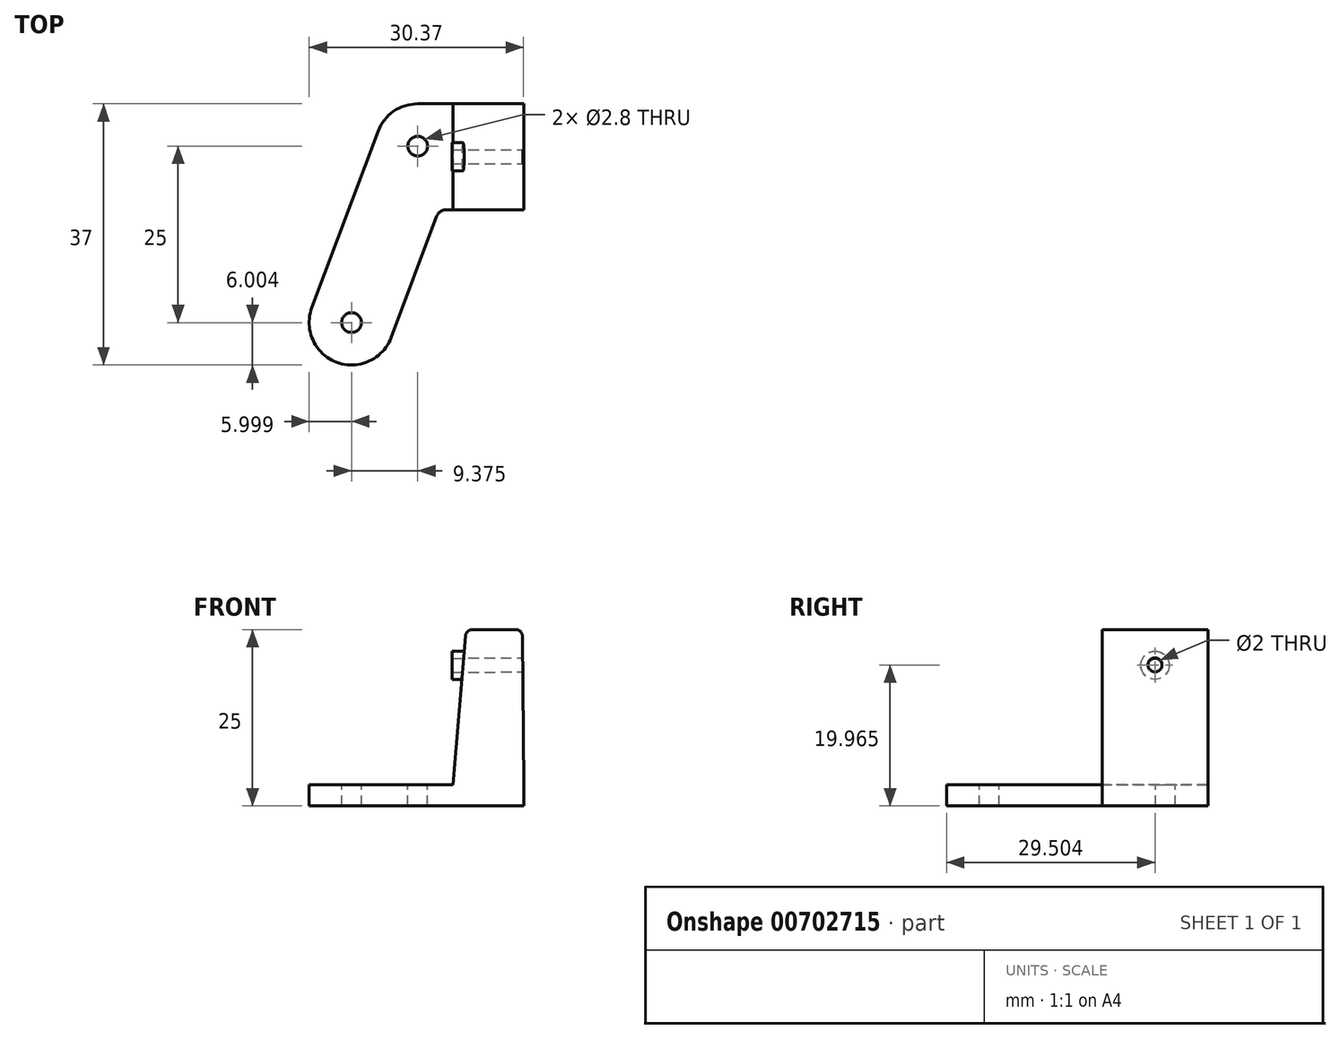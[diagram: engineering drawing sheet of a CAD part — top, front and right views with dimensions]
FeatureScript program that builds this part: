
annotation { "Feature Type Name" : "Feature", "Feature Type Description" : "" }
export const myFeature = defineFeature(function(context is Context, id is Id, definition is map)
    precondition{}
    {
        {
            var Q0;
            Q0=qCreatedBy(makeId("Top.planeOp"),FACE);
            var sketch = newSketch(context, id + "F0", { "sketchPlane" : qUnion([Q0])});
            skArc(sketch, "E0", {"start": v(4.1, -18.28) * mm, "mid": v(11.83, -21.8) * mm, "end": v(15.34, -14.07) * mm});
            skArc(sketch, "E1", {"start": v(5.96, 10.93) * mm, "mid": v(3.76, 13.76) * mm, "end": v(0.35, 14.82) * mm});
            skLineSegment(sketch, "E2", {"start": v(15.34, -14.07) * mm, "end": v(5.96, 10.93) * mm});
            skLineSegment(sketch, "E3", {"start": v(0.35, 14.82) * mm, "end": v(-14.65, 14.82) * mm});
            skLineSegment(sketch, "E4", {"start": v(-14.65, 14.82) * mm, "end": v(-14.65, -0.18) * mm});
            skLineSegment(sketch, "E5", {"start": v(9.72, -16.18) * mm, "end": v(0.35, 8.82) * mm, "construction": true});
            skLineSegment(sketch, "E6", {"start": v(4.1, -18.28) * mm, "end": v(-2.32, -1.15) * mm});
            skLineSegment(sketch, "E7", {"start": v(-14.65, -0.18) * mm, "end": v(-3.73, -0.18) * mm});
            skPoint(sketch, "E8.visualSharp", {"position": v(-2.69, -0.18) * mm});
            skArc(sketch, "E8.filletArc", {"start": v(-2.32, -1.15) * mm, "mid": v(-2.87, -0.44) * mm, "end": v(-3.73, -0.18) * mm});
            skCircle(sketch, "E9", {"center": v(0.35, 8.82) * mm, "radius": 1.4 * mm});
            skCircle(sketch, "E10", {"center": v(9.72, -16.18) * mm, "radius": 1.4 * mm});
            skLineSegment(sketch, "E11.0", {"start": v(-4.65, 14.82) * mm, "end": v(-4.65, -0.18) * mm});
            skSolve(sketch);
        }
        {
            var Q0;
            Q0=qCreatedBy(makeId("Top.planeOp"),FACE);
            cPlane(context, id + "F1", {"entities" : qUnion([Q0]), "cplaneType" : CPlaneType.OFFSET, "offset" : 22 * mm, "width" : 152.4 * mm, "height" : 152.4 * mm});
        }
        {
            var Q0;
            Q0=qCreatedBy(id+"F1.planeOp",FACE);
            var sketch = newSketch(context, id + "F2", { "sketchPlane" : qUnion([Q0])});
            skArc(sketch, "E12", {"start": v(4.26, -18.28) * mm, "mid": v(11.98, -21.8) * mm, "end": v(15.5, -14.07) * mm});
            skArc(sketch, "E13", {"start": v(6.12, 10.93) * mm, "mid": v(3.92, 13.76) * mm, "end": v(0.5, 14.82) * mm});
            skLineSegment(sketch, "E14", {"start": v(15.5, -14.07) * mm, "end": v(6.12, 10.93) * mm});
            skLineSegment(sketch, "E15", {"start": v(0.5, 14.82) * mm, "end": v(-14.5, 14.82) * mm});
            skLineSegment(sketch, "E16", {"start": v(-14.5, 14.82) * mm, "end": v(-14.5, -0.18) * mm});
            skLineSegment(sketch, "E17", {"start": v(9.87, -16.18) * mm, "end": v(0.5, 8.82) * mm, "construction": true});
            skLineSegment(sketch, "E18", {"start": v(4.26, -18.28) * mm, "end": v(-2.17, -1.15) * mm});
            skLineSegment(sketch, "E19", {"start": v(-14.5, -0.18) * mm, "end": v(-3.57, -0.18) * mm});
            skPoint(sketch, "E20.visualSharp", {"position": v(-2.53, -0.18) * mm});
            skArc(sketch, "E20.filletArc", {"start": v(-2.17, -1.15) * mm, "mid": v(-2.72, -0.44) * mm, "end": v(-3.57, -0.18) * mm});
            skCircle(sketch, "E21", {"center": v(0.5, 8.82) * mm, "radius": 1.4 * mm});
            skCircle(sketch, "E22", {"center": v(9.87, -16.18) * mm, "radius": 1.4 * mm});
            skLineSegment(sketch, "E23.0", {"start": v(-6.5, 14.82) * mm, "end": v(-6.5, -0.18) * mm});
            skSolve(sketch);
        }
        {
            var Q0;
            Q0=makeQuery(id+"F0.imprint","IMPRINT",FACE,{"disambiguationData":[TD([[makeQuery(id+"F0.imprint","IMPRINT",EDGE,{"derivedFrom":sQuery(id+"F0.wireOp",EDGE,"E0")}),1.0]])]});
            var Q1;
            {var subQ0=sQuery(id+"F0.wireOp",EDGE,"E4");Q1=makeQuery(id+"F0.imprint","IMPRINT",FACE,{"disambiguationData":[TD([[makeQuery(id+"F0.imprint","IMPRINT",EDGE,{"derivedFrom":subQ0}),1.0]])]});}
            extrude(context, id + "F3", {"entities" : qUnion([Q0, Q1]), "oppositeDirection" : true, "depth" : 3 * mm, "offsetDistance" : 25.4 * mm});
        }
        {
            var Q1;
            {var subQ0=sQuery(id+"F0.wireOp",EDGE,"E4");Q1=makeQuery(id+"F0.imprint","IMPRINT",FACE,{"disambiguationData":[TD([[makeQuery(id+"F0.imprint","IMPRINT",EDGE,{"derivedFrom":subQ0}),1.0]])]});}
            var Q2;
            {var subQ0=sQuery(id+"F2.wireOp",EDGE,"E16");Q2=makeQuery(id+"F2.imprint","IMPRINT",FACE,{"disambiguationData":[TD([[makeQuery(id+"F2.imprint","IMPRINT",EDGE,{"derivedFrom":subQ0}),1.0]])]});}
            loft(context, id + "F4", {"operationType" : NewBodyOperationType.ADD, "sheetProfilesArray" : [{ "sheetProfileEntities" : qUnion([Q1]) }, { "sheetProfileEntities" : qUnion([Q2]) }]});
        }
        {
            var Q0;
            Q0=makeQuery(id+"F4.opLoft","SWEPT_FACE",FACE,{"disambiguationData":[OSD([sQuery(id+"F0.wireOp",EDGE,"E3"),sQuery(id+"F0.wireOp",EDGE,"E4"),sQuery(id+"F0.wireOp",EDGE,"E7"),sQuery(id+"F2.wireOp",EDGE,"E15"),sQuery(id+"F2.wireOp",EDGE,"E16"),sQuery(id+"F2.wireOp",EDGE,"E19")])]});
            var sketch = newSketch(context, id + "F5", { "sketchPlane" : qUnion([Q0])});
            skCircle(sketch, "E24", {"center": v(-7.32, 16.9) * mm, "radius": 1 * mm});
            skCircle(sketch, "E25", {"center": v(-7.32, 16.9) * mm, "radius": 2 * mm});
            skSolve(sketch);
        }
        {
            var Q0;
            Q0=makeQuery(id+"F5.imprint","IMPRINT",FACE,{"disambiguationData":[TD([[makeQuery(id+"F5.imprint","IMPRINT",EDGE,{"derivedFrom":sQuery(id+"F5.wireOp",EDGE,"E24")}),-1.0]])]});
            extrude(context, id + "F6", {"entities" : qUnion([Q0]), "operationType" : NewBodyOperationType.ADD, "oppositeDirection" : true, "depth" : 10 * mm, "offsetDistance" : 25.4 * mm});
        }
        {
            var Q0;
            Q0=makeQuery(id+"F5.imprint","IMPRINT",FACE,{"disambiguationData":[TD([[makeQuery(id+"F5.imprint","IMPRINT",EDGE,{"derivedFrom":sQuery(id+"F5.wireOp",EDGE,"E24")}),1.0]])]});
            extrude(context, id + "F7", {"entities" : qUnion([Q0]), "operationType" : NewBodyOperationType.REMOVE, "oppositeDirection" : true, "depth" : 15 * mm, "offsetDistance" : 25.4 * mm});
        }
        {
            var Q0;
            Q0=makeQuery(id+"F4.opLoft","MID_CAP_EDGE",EDGE,{"disambiguationData":[OSD([sQuery(id+"F2.wireOp",EDGE,"E15"),sQuery(id+"F2.wireOp",EDGE,"E19"),sQuery(id+"F2.wireOp",EDGE,"E23.0")])],"capPos":1.0});
            var Q1;
            Q1=makeQuery(id+"F4.opLoft","MID_CAP_EDGE",EDGE,{"disambiguationData":[OSD([sQuery(id+"F2.wireOp",EDGE,"E15"),sQuery(id+"F2.wireOp",EDGE,"E16"),sQuery(id+"F2.wireOp",EDGE,"E19")])],"capPos":1.0});
            var Q2;
            Q2=makeQuery(id+"F4.opLoft","MID_CAP_EDGE",EDGE,{"disambiguationData":[OSD([sQuery(id+"F0.wireOp",EDGE,"E3"),sQuery(id+"F0.wireOp",EDGE,"E7"),sQuery(id+"F0.wireOp",EDGE,"E11.0")])],"capPos":0.0});
            fillet(context, id + "F8", {"entities" : qUnion([Q0, Q1, Q2]), "radius" : 1 * mm, "tangentPropagation" : true, "allowEdgeOverflow" : false});
        }
        {
            var Q0;
            Q0=makeQuery(id+"F3.opExtrude","SWEPT_BODY",BODY,{"disambiguationData":[OSD([sQuery(id+"F0.wireOp",EDGE,"E0"),sQuery(id+"F0.wireOp",EDGE,"E1"),sQuery(id+"F0.wireOp",EDGE,"E2"),sQuery(id+"F0.wireOp",EDGE,"E3"),sQuery(id+"F0.wireOp",EDGE,"E4"),sQuery(id+"F0.wireOp",EDGE,"E6"),sQuery(id+"F0.wireOp",EDGE,"E7"),sQuery(id+"F0.wireOp",EDGE,"E8.filletArc"),sQuery(id+"F0.wireOp",EDGE,"E9"),sQuery(id+"F0.wireOp",EDGE,"E10")])]});
            var Q1;
            Q1=qCreatedBy(makeId("Right.planeOp"),FACE);
            mirror(context, id + "F9", {"entities" : qUnion([Q0]), "mirrorPlane" : qUnion([Q1])});
        }
        {
            var Q0;
            Q0=makeQuery(id+"F3.opExtrude","SWEPT_BODY",BODY,{"disambiguationData":[OSD([sQuery(id+"F0.wireOp",EDGE,"E0"),sQuery(id+"F0.wireOp",EDGE,"E1"),sQuery(id+"F0.wireOp",EDGE,"E2"),sQuery(id+"F0.wireOp",EDGE,"E3"),sQuery(id+"F0.wireOp",EDGE,"E4"),sQuery(id+"F0.wireOp",EDGE,"E6"),sQuery(id+"F0.wireOp",EDGE,"E7"),sQuery(id+"F0.wireOp",EDGE,"E8.filletArc"),sQuery(id+"F0.wireOp",EDGE,"E9"),sQuery(id+"F0.wireOp",EDGE,"E10")])]});
            deleteBodies(context, id + "F10", {"entities" : qUnion([Q0])});
        }
    });
